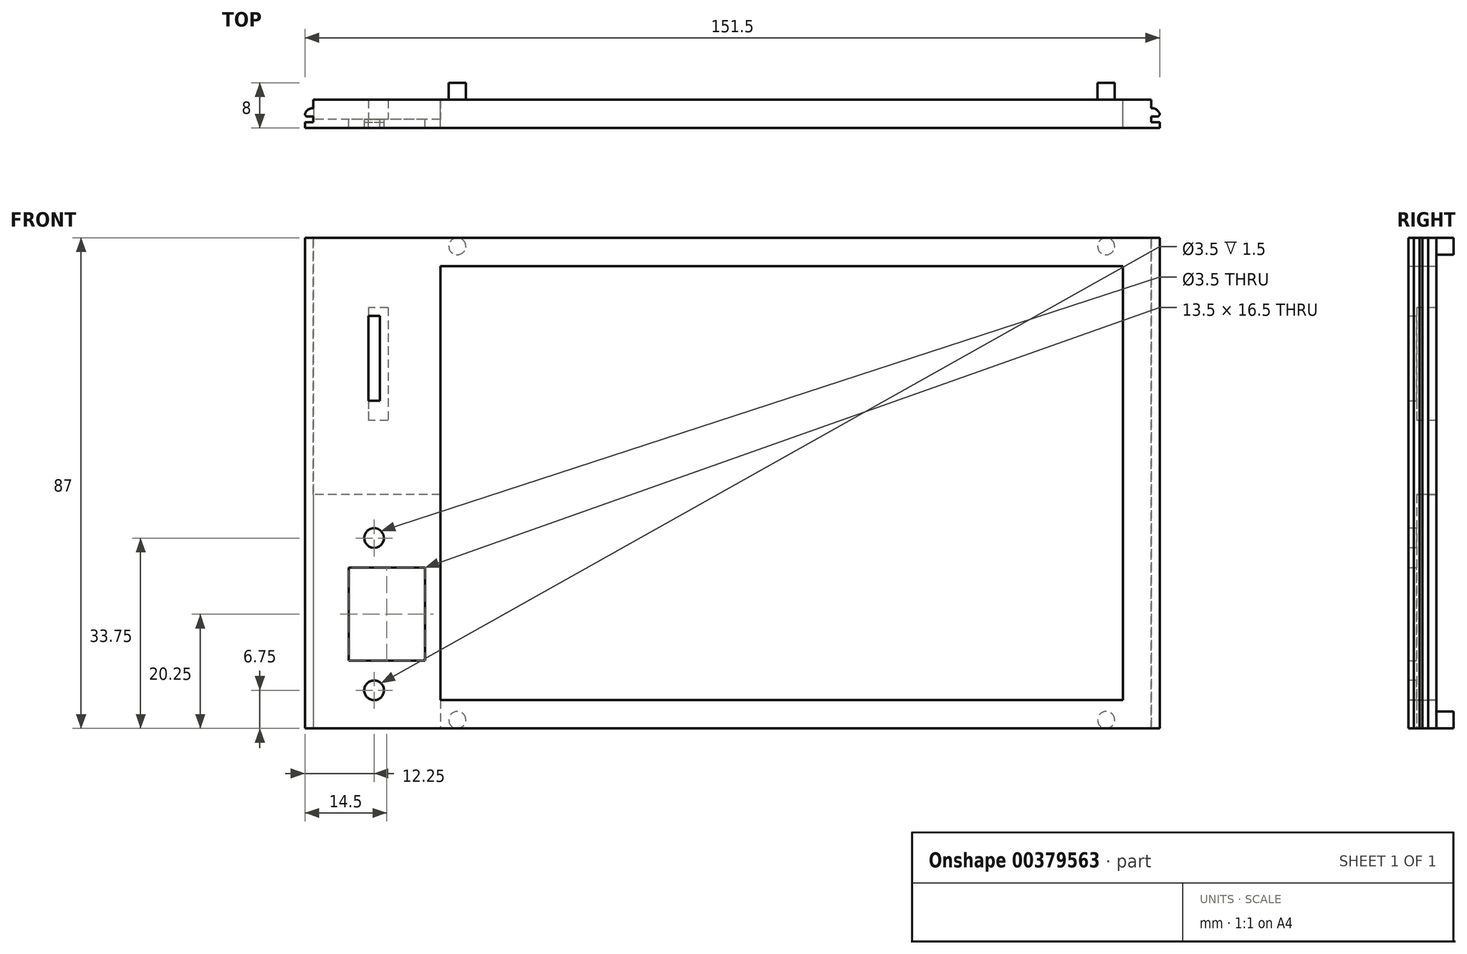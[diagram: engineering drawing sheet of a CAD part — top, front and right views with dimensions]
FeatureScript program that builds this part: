
annotation { "Feature Type Name" : "Feature", "Feature Type Description" : "" }
export const myFeature = defineFeature(function(context is Context, id is Id, definition is map)
    precondition{}
    {
        {
            var Q0;
            Q0=qCreatedBy(makeId("Front.planeOp"),FACE);
            var sketch = newSketch(context, id + "F0", { "sketchPlane" : qUnion([Q0])});
            skLineSegment(sketch, "E0.bottom", {"start": v(72.55, -42.1) * mm, "end": v(-75.95, -42.1) * mm});
            skLineSegment(sketch, "E0.top", {"start": v(72.55, 44.9) * mm, "end": v(-75.95, 44.9) * mm});
            skLineSegment(sketch, "E0.left", {"start": v(72.55, -42.1) * mm, "end": v(72.55, 44.9) * mm});
            skLineSegment(sketch, "E0.right", {"start": v(-75.95, -42.1) * mm, "end": v(-75.95, 44.9) * mm});
            skLineSegment(sketch, "E1.bottom", {"start": v(67.55, -37.1) * mm, "end": v(-53.45, -37.1) * mm});
            skLineSegment(sketch, "E1.top", {"start": v(67.55, 39.9) * mm, "end": v(-53.45, 39.9) * mm});
            skLineSegment(sketch, "E1.left", {"start": v(67.55, -37.1) * mm, "end": v(67.55, 39.9) * mm});
            skLineSegment(sketch, "E1.right", {"start": v(-53.45, -37.1) * mm, "end": v(-53.45, 39.9) * mm});
            skLineSegment(sketch, "E2.bottom", {"start": v(-69.7, -13.6) * mm, "end": v(-56.2, -13.6) * mm});
            skLineSegment(sketch, "E2.top", {"start": v(-69.7, -30.1) * mm, "end": v(-56.2, -30.1) * mm});
            skLineSegment(sketch, "E2.left", {"start": v(-69.7, -13.6) * mm, "end": v(-69.7, -30.1) * mm});
            skLineSegment(sketch, "E2.right", {"start": v(-56.2, -13.6) * mm, "end": v(-56.2, -30.1) * mm});
            skCircle(sketch, "E3", {"center": v(-65.2, -8.35) * mm, "radius": 1.75 * mm});
            skCircle(sketch, "E4.MirrorC", {"center": v(-65.2, -35.35) * mm, "radius": 1.75 * mm});
            skLineSegment(sketch, "E5", {"start": v(-65.2, 60.4) * mm, "end": v(-65.2, -47.79) * mm, "construction": true});
            skLineSegment(sketch, "E6.bottom", {"start": v(-66.2, 31.04) * mm, "end": v(-64.2, 31.04) * mm});
            skLineSegment(sketch, "E6.top", {"start": v(-66.2, 16.04) * mm, "end": v(-64.2, 16.04) * mm});
            skLineSegment(sketch, "E6.left", {"start": v(-66.2, 31.04) * mm, "end": v(-66.2, 16.04) * mm});
            skLineSegment(sketch, "E6.right", {"start": v(-64.2, 31.04) * mm, "end": v(-64.2, 16.04) * mm});
            skLineSegment(sketch, "E7", {"start": v(79.54, 43.44) * mm, "end": v(-81.76, 43.44) * mm, "construction": true});
            skSolve(sketch);
        }
        {
            var Q0;
            Q0=makeQuery(id+"F0.imprint","IMPRINT",FACE,{"disambiguationData":[TD([[makeQuery(id+"F0.imprint","IMPRINT",EDGE,{"derivedFrom":sQuery(id+"F0.wireOp",EDGE,"E0.bottom")}),-1.0]])]});
            extrude(context, id + "F1", {"entities" : qUnion([Q0]), "oppositeDirection" : true, "depth" : 5 * mm, "offsetDistance" : 25 * mm});
        }
        {
            var Q0;
            Q0=qCreatedBy(makeId("Front.planeOp"),FACE);
            var sketch = newSketch(context, id + "F2", { "sketchPlane" : qUnion([Q0])});
            skLineSegment(sketch, "E8.bottom", {"start": v(-77.45, 44.9) * mm, "end": v(74.05, 44.9) * mm});
            skLineSegment(sketch, "E8.top", {"start": v(-77.45, -42.1) * mm, "end": v(74.05, -42.1) * mm});
            skLineSegment(sketch, "E8.left", {"start": v(-77.45, 44.9) * mm, "end": v(-77.45, -42.1) * mm});
            skLineSegment(sketch, "E8.right", {"start": v(74.05, 44.9) * mm, "end": v(74.05, -42.1) * mm});
            skLineSegment(sketch, "E9.bottom", {"start": v(-69.7, -13.6) * mm, "end": v(-56.2, -13.6) * mm});
            skLineSegment(sketch, "E9.top", {"start": v(-69.7, -30.1) * mm, "end": v(-56.2, -30.1) * mm});
            skLineSegment(sketch, "E9.left", {"start": v(-69.7, -13.6) * mm, "end": v(-69.7, -30.1) * mm});
            skLineSegment(sketch, "E9.right", {"start": v(-56.2, -13.6) * mm, "end": v(-56.2, -30.1) * mm});
            skCircle(sketch, "E10", {"center": v(-65.2, -8.35) * mm, "radius": 1.75 * mm});
            skCircle(sketch, "E11.MirrorC", {"center": v(-65.2, -35.34) * mm, "radius": 1.75 * mm});
            skLineSegment(sketch, "E12.bottom", {"start": v(-66.2, 31.04) * mm, "end": v(-64.2, 31.04) * mm});
            skLineSegment(sketch, "E12.top", {"start": v(-66.2, 16.04) * mm, "end": v(-64.2, 16.04) * mm});
            skLineSegment(sketch, "E12.left", {"start": v(-66.2, 31.04) * mm, "end": v(-66.2, 16.04) * mm});
            skLineSegment(sketch, "E12.right", {"start": v(-64.2, 31.04) * mm, "end": v(-64.2, 16.04) * mm});
            skLineSegment(sketch, "E13.bottom", {"start": v(67.55, -37.1) * mm, "end": v(-53.45, -37.1) * mm});
            skLineSegment(sketch, "E13.top", {"start": v(67.55, 39.9) * mm, "end": v(-53.45, 39.9) * mm});
            skLineSegment(sketch, "E13.left", {"start": v(67.55, -37.1) * mm, "end": v(67.55, 39.9) * mm});
            skLineSegment(sketch, "E13.right", {"start": v(-53.45, -37.1) * mm, "end": v(-53.45, 39.9) * mm});
            skSolve(sketch);
        }
        {
            var Q0;
            Q0 = qSketchRegion(id + "F2", true);
            extrude(context, id + "F3", {"entities" : qUnion([Q0]), "operationType" : NewBodyOperationType.ADD, "oppositeDirection" : true, "depth" : 1 * mm, "offsetDistance" : 25 * mm});
        }
        {
            var Q0;
            Q0=qCreatedBy(makeId("Front.planeOp"),FACE);
            var sketch = newSketch(context, id + "F4", { "sketchPlane" : qUnion([Q0])});
            skLineSegment(sketch, "E14.bottom", {"start": v(-53.45, -0.63) * mm, "end": v(-75.95, -0.63) * mm});
            skLineSegment(sketch, "E14.top", {"start": v(-53.45, -42.1) * mm, "end": v(-75.95, -42.1) * mm});
            skLineSegment(sketch, "E14.left", {"start": v(-53.45, -0.63) * mm, "end": v(-53.45, -42.1) * mm});
            skLineSegment(sketch, "E14.right", {"start": v(-75.95, -0.63) * mm, "end": v(-75.95, -42.1) * mm});
            skSolve(sketch);
        }
        {
            var Q0;
            Q0=qCreatedBy(makeId("Front.planeOp"),FACE);
            var sketch = newSketch(context, id + "F5", { "sketchPlane" : qUnion([Q0])});
            skLineSegment(sketch, "E15.bottom", {"start": v(-62.7, 32.54) * mm, "end": v(-66.2, 32.54) * mm});
            skLineSegment(sketch, "E15.top", {"start": v(-62.7, 12.54) * mm, "end": v(-66.2, 12.54) * mm});
            skLineSegment(sketch, "E15.left", {"start": v(-62.7, 32.54) * mm, "end": v(-62.7, 12.54) * mm});
            skLineSegment(sketch, "E15.right", {"start": v(-66.2, 32.54) * mm, "end": v(-66.2, 12.54) * mm});
            skSolve(sketch);
        }
        {
            var Q0;
            Q0 = qSketchRegion(id + "F2", true);
            extrude(context, id + "F6", {"entities" : qUnion([Q0]), "operationType" : NewBodyOperationType.ADD, "oppositeDirection" : true, "depth" : 3.5 * mm, "offsetDistance" : 25 * mm, "hasSecondDirection" : true, "secondDirectionOppositeDirection" : true, "secondDirectionDepth" : 2 * mm});
        }
        {
            var Q0;
            Q0 = qSketchRegion(id + "F5", true);
            extrude(context, id + "F7", {"entities" : qUnion([Q0]), "operationType" : NewBodyOperationType.REMOVE, "oppositeDirection" : true, "depth" : 22 * mm, "offsetDistance" : 25 * mm, "hasSecondDirection" : true, "secondDirectionOppositeDirection" : true, "secondDirectionDepth" : 1.5 * mm});
        }
        {
            var Q0;
            Q0 = qSketchRegion(id + "F4", true);
            extrude(context, id + "F8", {"entities" : qUnion([Q0]), "operationType" : NewBodyOperationType.REMOVE, "oppositeDirection" : true, "depth" : 22 * mm, "offsetDistance" : 25 * mm, "hasSecondDirection" : true, "secondDirectionOppositeDirection" : true, "secondDirectionDepth" : 1.5 * mm});
        }
        {
            var Q0;
            Q0=qCreatedBy(makeId("Front.planeOp"),FACE);
            var sketch = newSketch(context, id + "F9", { "sketchPlane" : qUnion([Q0])});
            skLineSegment(sketch, "E16", {"start": v(64.55, 57) * mm, "end": v(64.55, -54.93) * mm, "construction": true});
            skLineSegment(sketch, "E17", {"start": v(-50.45, 54.3) * mm, "end": v(-50.45, -55.44) * mm, "construction": true});
            skLineSegment(sketch, "E18", {"start": v(80.65, 43.4) * mm, "end": v(-83.14, 43.4) * mm, "construction": true});
            skLineSegment(sketch, "E19", {"start": v(80.9, -40.6) * mm, "end": v(-82.9, -40.6) * mm, "construction": true});
            skCircle(sketch, "E20", {"center": v(64.55, 43.4) * mm, "radius": 1.5 * mm});
            skCircle(sketch, "E21", {"center": v(64.55, -40.6) * mm, "radius": 1.5 * mm});
            skCircle(sketch, "E22", {"center": v(-50.45, -40.6) * mm, "radius": 1.5 * mm});
            skCircle(sketch, "E23", {"center": v(-50.45, 43.4) * mm, "radius": 1.5 * mm});
            skSolve(sketch);
        }
        {
            var Q0;
            Q0 = qSketchRegion(id + "F9", true);
            extrude(context, id + "F10", {"entities" : qUnion([Q0]), "operationType" : NewBodyOperationType.ADD, "oppositeDirection" : true, "depth" : 8 * mm, "offsetDistance" : 25 * mm});
        }
        {
            var Q0;
            Q0=makeQuery(id+"F6.opExtrude","CAP_EDGE",EDGE,{"disambiguationData":[OSD([sQuery(id+"F2.wireOp",EDGE,"E8.right")])],"isStart":true});
            fillet(context, id + "F11", {"entities" : qUnion([Q0]), "radius" : 0.5 * mm, "allowEdgeOverflow" : false});
        }
        {
            var Q0;
            Q0=makeQuery(id+"F6.opExtrude","CAP_EDGE",EDGE,{"disambiguationData":[OSD([sQuery(id+"F2.wireOp",EDGE,"E8.left")])],"isStart":true});
            fillet(context, id + "F12", {"entities" : qUnion([Q0]), "radius" : 0.5 * mm, "tangentPropagation" : true, "allowEdgeOverflow" : false});
        }
        {
            var Q0;
            Q0=makeQuery(id+"F6.opExtrude","CAP_EDGE",EDGE,{"disambiguationData":[OSD([sQuery(id+"F2.wireOp",EDGE,"E8.right")])],"isStart":false});
            fillet(context, id + "F13", {"entities" : qUnion([Q0]), "radius" : 1.5 * mm, "tangentPropagation" : true, "allowEdgeOverflow" : false});
        }
        {
            var Q0;
            Q0=makeQuery(id+"F6.opExtrude","CAP_EDGE",EDGE,{"disambiguationData":[OSD([sQuery(id+"F2.wireOp",EDGE,"E8.left")])],"isStart":false});
            fillet(context, id + "F14", {"entities" : qUnion([Q0]), "radius" : 1.5 * mm, "tangentPropagation" : true, "allowEdgeOverflow" : false});
        }
    });
